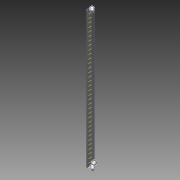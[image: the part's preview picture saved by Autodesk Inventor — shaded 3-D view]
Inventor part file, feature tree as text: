
AUTODESK INVENTOR PART (.ipt)
format: ipt  version: 2015 (Build 190159000, 159)  size: 459,264 bytes
history: native  units: in
note: dims shown in document units (in); Inventor stores cm internally (conversion verified against a paired STEP export)
features: other x39, boolean_combine x1, extrude x1, pattern_linear x1, imported_body x1, sketch x1
ambient origin geometry x8: Origin, YZ Plane, XZ Plane, XY Plane, X Axis, Y Axis, Z Axis, Center Point
bodies: Body1 (feature_tree)
feature tree (44):
  boolean_combine  "Combine1"
  other  "Linear Slide"
  other  "Work Axis1"
  extrude  "Extrusion1"  TaperAngle=0.0deg  [1 undecoded]
  pattern_linear  "Rectangular Pattern1"  Spacing1=0.0in  [1 undecoded]
  other  "bottom plane"
  other  "top plane"
  imported_body  "Base1"
  other  "Work Point1"
  other  "Work Axis2"
  sketch  "Sketch1"  dims[d0=13.7795in d2=0.5in d4=0.0in d5=0.0in d6=0.0in d8=0.0in]
  other  "Work Axis46"
  other  "Work Axis47"
  other  "Work Axis48"
  other  "Work Axis49"
  other  "Work Axis50"
  other  "Work Axis51"
  other  "Work Axis52"
  other  "Work Axis53"
  other  "Work Axis54"
  other  "Work Axis55"
  other  "Work Axis56"
  other  "Work Axis57"
  other  "Work Axis69"
  other  "Work Axis70"
  other  "Work Axis71"
  other  "Work Axis72"
  other  "Work Axis73"
  other  "Work Axis74"
  other  "Work Axis75"
  other  "Work Axis76"
  other  "Work Axis77"
  other  "Work Axis78"
  other  "Work Axis90"
  other  "Work Axis91"
  other  "Work Axis92"
  other  "Work Axis93"
  other  "Work Axis94"
  other  "Work Axis95"
  other  "Work Axis96"
  other  "Work Axis97"
  other  "Work Axis98"
  other  "Work Axis99"
  other  "Work Axis100"
note: 2 required parameter values undecoded (feature->parameter linkage not recoverable at this tier; creation-order binding heuristic only, values carry confidence <= 0.55)
